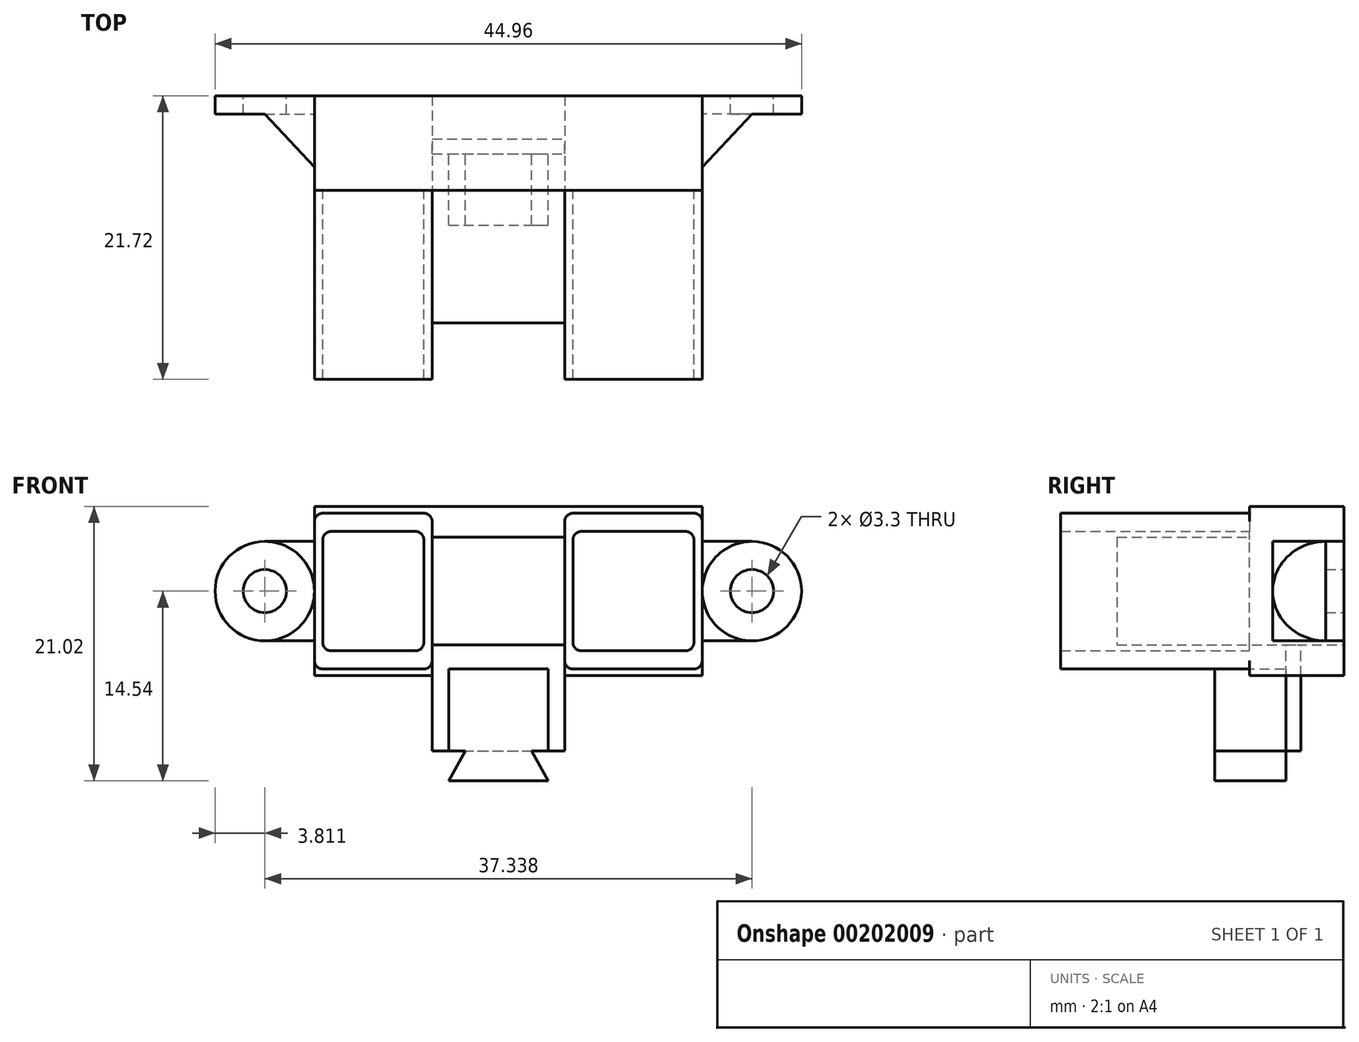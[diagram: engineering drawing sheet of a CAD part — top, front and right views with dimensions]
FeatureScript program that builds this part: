
annotation { "Feature Type Name" : "Feature", "Feature Type Description" : "" }
export const myFeature = defineFeature(function(context is Context, id is Id, definition is map)
    precondition{}
    {
        {
            var Q0;
            Q0=qCreatedBy(makeId("Front.planeOp"),FACE);
            var sketch = newSketch(context, id + "F0", { "sketchPlane" : qUnion([Q0])});
            skLineSegment(sketch, "E0.bottom", {"start": v(-14.86, 6.48) * mm, "end": v(14.86, 6.48) * mm});
            skLineSegment(sketch, "E0.top", {"start": v(-14.86, -6.48) * mm, "end": v(14.86, -6.48) * mm});
            skLineSegment(sketch, "E0.left", {"start": v(-14.86, 6.48) * mm, "end": v(-14.86, -6.48) * mm});
            skLineSegment(sketch, "E0.right", {"start": v(14.86, 6.48) * mm, "end": v(14.86, -6.48) * mm});
            skPoint(sketch, "E0.middle", {"position": v(0, 0) * mm});
            skSolve(sketch);
        }
        {
            var Q0;
            Q0=makeQuery(id+"F0.imprint","IMPRINT",FACE,{"disambiguationData":[TD([[makeQuery(id+"F0.imprint","IMPRINT",EDGE,{"derivedFrom":sQuery(id+"F0.wireOp",EDGE,"E0.bottom")}),-1.0]])]});
            extrude(context, id + "F1", {"entities" : qUnion([Q0]), "oppositeDirection" : true, "depth" : 7.24 * mm});
        }
        {
            var Q0;
            Q0=makeQuery(id+"F1.opExtrude","CAP_FACE",FACE,{"disambiguationData":[OSD([sQuery(id+"F0.wireOp",EDGE,"E0.bottom"),sQuery(id+"F0.wireOp",EDGE,"E0.top"),sQuery(id+"F0.wireOp",EDGE,"E0.left"),sQuery(id+"F0.wireOp",EDGE,"E0.right")])],"isStart":true});
            var sketch = newSketch(context, id + "F2", { "sketchPlane" : qUnion([Q0])});
            skLineSegment(sketch, "E1.bottom", {"start": v(-14.22, 5.97) * mm, "end": v(-6.48, 5.97) * mm});
            skLineSegment(sketch, "E1.top", {"start": v(-14.22, -5.97) * mm, "end": v(-6.48, -5.97) * mm});
            skLineSegment(sketch, "E1.left", {"start": v(-14.86, 5.33) * mm, "end": v(-14.86, -5.33) * mm});
            skLineSegment(sketch, "E1.right", {"start": v(-5.84, 5.33) * mm, "end": v(-5.84, -5.33) * mm});
            skPoint(sketch, "E2.visualSharp", {"position": v(-14.86, 5.97) * mm});
            skArc(sketch, "E2.filletArc", {"start": v(-14.22, 5.97) * mm, "mid": v(-14.67, 5.78) * mm, "end": v(-14.86, 5.33) * mm});
            skPoint(sketch, "E3.visualSharp", {"position": v(-5.84, 5.97) * mm});
            skArc(sketch, "E3.filletArc", {"start": v(-5.84, 5.33) * mm, "mid": v(-6.03, 5.78) * mm, "end": v(-6.48, 5.97) * mm});
            skPoint(sketch, "E4.visualSharp", {"position": v(-14.86, -5.97) * mm});
            skArc(sketch, "E4.filletArc", {"start": v(-14.86, -5.33) * mm, "mid": v(-14.67, -5.78) * mm, "end": v(-14.22, -5.97) * mm});
            skPoint(sketch, "E5.visualSharp", {"position": v(-5.84, -5.97) * mm});
            skArc(sketch, "E5.filletArc", {"start": v(-6.48, -5.97) * mm, "mid": v(-6.03, -5.78) * mm, "end": v(-5.84, -5.33) * mm});
            skLineSegment(sketch, "E6", {"start": v(-14.22, 3.94) * mm, "end": v(-14.22, -3.94) * mm});
            skLineSegment(sketch, "E7", {"start": v(-13.59, -4.57) * mm, "end": v(-7.11, -4.57) * mm});
            skLineSegment(sketch, "E8", {"start": v(-6.48, -3.94) * mm, "end": v(-6.48, 3.94) * mm});
            skLineSegment(sketch, "E9", {"start": v(-13.59, 4.57) * mm, "end": v(-7.11, 4.57) * mm});
            skPoint(sketch, "E10.visualSharp", {"position": v(-14.22, 4.57) * mm});
            skArc(sketch, "E10.filletArc", {"start": v(-13.59, 4.57) * mm, "mid": v(-14.04, 4.39) * mm, "end": v(-14.22, 3.94) * mm});
            skPoint(sketch, "E11.visualSharp", {"position": v(-6.48, 4.57) * mm});
            skArc(sketch, "E11.filletArc", {"start": v(-6.48, 3.94) * mm, "mid": v(-6.66, 4.39) * mm, "end": v(-7.11, 4.57) * mm});
            skPoint(sketch, "E12.visualSharp", {"position": v(-6.48, -4.57) * mm});
            skArc(sketch, "E12.filletArc", {"start": v(-7.11, -4.57) * mm, "mid": v(-6.66, -4.39) * mm, "end": v(-6.48, -3.94) * mm});
            skPoint(sketch, "E13.visualSharp", {"position": v(-14.22, -4.57) * mm});
            skArc(sketch, "E13.filletArc", {"start": v(-14.22, -3.94) * mm, "mid": v(-14.04, -4.39) * mm, "end": v(-13.59, -4.57) * mm});
            skSolve(sketch);
        }
        {
            var Q0;
            Q0=makeQuery(id+"F2.imprint","IMPRINT",FACE,{"disambiguationData":[TD([[makeQuery(id+"F2.imprint","IMPRINT",EDGE,{"derivedFrom":sQuery(id+"F2.wireOp",EDGE,"E1.bottom")}),-1.0]])]});
            extrude(context, id + "F3", {"entities" : qUnion([Q0]), "operationType" : NewBodyOperationType.ADD, "depth" : 14.48 * mm});
        }
        {
            var Q0;
            {var subQ0=sQuery(id+"F0.wireOp",EDGE,"E0.top");var subQ1=sQuery(id+"F0.wireOp",EDGE,"E0.bottom");var subQ2=sQuery(id+"F0.wireOp",EDGE,"E0.left");var subQ3=sQuery(id+"F0.wireOp",EDGE,"E0.right");Q0=makeQuery(id+"F3.boolean.opBoolean","SPLIT",FACE,{"disambiguationData":[TD([makeQuery(id+"F1.opExtrude","SWEPT_FACE",FACE,{"disambiguationData":[OSD([subQ1])]})])],"derivedFrom":makeQuery(id+"F1.opExtrude","CAP_FACE",FACE,{"disambiguationData":[OSD([subQ1,subQ0,subQ2,subQ3])],"isStart":true})});}
            var sketch = newSketch(context, id + "F4", { "sketchPlane" : qUnion([Q0])});
            skLineSegment(sketch, "E14.bottom", {"start": v(4.95, 5.97) * mm, "end": v(14.22, 5.97) * mm});
            skLineSegment(sketch, "E14.top", {"start": v(4.95, -5.97) * mm, "end": v(14.22, -5.97) * mm});
            skLineSegment(sketch, "E14.left", {"start": v(4.32, 5.33) * mm, "end": v(4.32, -5.33) * mm});
            skLineSegment(sketch, "E14.right", {"start": v(14.86, 5.33) * mm, "end": v(14.86, -5.33) * mm});
            skPoint(sketch, "E15.visualSharp", {"position": v(4.32, 5.97) * mm});
            skArc(sketch, "E15.filletArc", {"start": v(4.95, 5.97) * mm, "mid": v(4.5, 5.78) * mm, "end": v(4.32, 5.33) * mm});
            skPoint(sketch, "E16.visualSharp", {"position": v(14.86, 5.97) * mm});
            skArc(sketch, "E16.filletArc", {"start": v(14.86, 5.33) * mm, "mid": v(14.67, 5.78) * mm, "end": v(14.22, 5.97) * mm});
            skPoint(sketch, "E17.visualSharp", {"position": v(14.86, -5.97) * mm});
            skArc(sketch, "E17.filletArc", {"start": v(14.22, -5.97) * mm, "mid": v(14.67, -5.78) * mm, "end": v(14.86, -5.33) * mm});
            skPoint(sketch, "E18.visualSharp", {"position": v(4.32, -5.97) * mm});
            skArc(sketch, "E18.filletArc", {"start": v(4.32, -5.33) * mm, "mid": v(4.5, -5.78) * mm, "end": v(4.95, -5.97) * mm});
            skLineSegment(sketch, "E19", {"start": v(5.59, 4.57) * mm, "end": v(13.59, 4.57) * mm});
            skLineSegment(sketch, "E20", {"start": v(14.22, 3.94) * mm, "end": v(14.22, -3.94) * mm});
            skLineSegment(sketch, "E21", {"start": v(13.59, -4.57) * mm, "end": v(5.59, -4.57) * mm});
            skLineSegment(sketch, "E22", {"start": v(4.95, -3.94) * mm, "end": v(4.95, 3.94) * mm});
            skPoint(sketch, "E23.visualSharp", {"position": v(4.95, 4.57) * mm});
            skArc(sketch, "E23.filletArc", {"start": v(5.59, 4.57) * mm, "mid": v(5.14, 4.39) * mm, "end": v(4.95, 3.94) * mm});
            skPoint(sketch, "E24.visualSharp", {"position": v(14.22, 4.57) * mm});
            skArc(sketch, "E24.filletArc", {"start": v(14.22, 3.94) * mm, "mid": v(14.04, 4.39) * mm, "end": v(13.59, 4.57) * mm});
            skPoint(sketch, "E25.visualSharp", {"position": v(14.22, -4.57) * mm});
            skArc(sketch, "E25.filletArc", {"start": v(13.59, -4.57) * mm, "mid": v(14.04, -4.39) * mm, "end": v(14.22, -3.94) * mm});
            skPoint(sketch, "E26.visualSharp", {"position": v(4.95, -4.57) * mm});
            skArc(sketch, "E26.filletArc", {"start": v(4.95, -3.94) * mm, "mid": v(5.14, -4.39) * mm, "end": v(5.59, -4.57) * mm});
            skSolve(sketch);
        }
        {
            var Q0;
            Q0=makeQuery(id+"F4.imprint","IMPRINT",FACE,{"disambiguationData":[TD([[makeQuery(id+"F4.imprint","IMPRINT",EDGE,{"derivedFrom":sQuery(id+"F4.wireOp",EDGE,"E14.bottom")}),-1.0]])]});
            var Q1;
            Q1=makeQuery(id+"F3.opExtrude","CAP_FACE",FACE,{"disambiguationData":[OSD([sQuery(id+"F2.wireOp",EDGE,"E1.bottom"),sQuery(id+"F2.wireOp",EDGE,"E1.top"),sQuery(id+"F2.wireOp",EDGE,"E1.left"),sQuery(id+"F2.wireOp",EDGE,"E1.right"),sQuery(id+"F2.wireOp",EDGE,"E2.filletArc"),sQuery(id+"F2.wireOp",EDGE,"E3.filletArc"),sQuery(id+"F2.wireOp",EDGE,"E4.filletArc"),sQuery(id+"F2.wireOp",EDGE,"E5.filletArc"),sQuery(id+"F2.wireOp",EDGE,"E6"),sQuery(id+"F2.wireOp",EDGE,"E7"),sQuery(id+"F2.wireOp",EDGE,"E8"),sQuery(id+"F2.wireOp",EDGE,"E9"),sQuery(id+"F2.wireOp",EDGE,"E10.filletArc"),sQuery(id+"F2.wireOp",EDGE,"E11.filletArc"),sQuery(id+"F2.wireOp",EDGE,"E12.filletArc"),sQuery(id+"F2.wireOp",EDGE,"E13.filletArc")])],"isStart":false});
            extrude(context, id + "F5", {"entities" : qUnion([Q0]), "operationType" : NewBodyOperationType.ADD, "endBound" : BoundingType.UP_TO_SURFACE, "endBoundEntityFace" : qUnion([Q1]), "depth" : 25.4 * mm});
        }
        {
            var Q0;
            {var subQ5=sQuery(id+"F0.wireOp",EDGE,"E0.bottom");var subQ6=makeQuery(id+"F1.opExtrude","SWEPT_FACE",FACE,{"disambiguationData":[OSD([subQ5])]});var subQ8=sQuery(id+"F0.wireOp",EDGE,"E0.right");var subQ10=sQuery(id+"F0.wireOp",EDGE,"E0.top");var subQ12=sQuery(id+"F0.wireOp",EDGE,"E0.left");Q0=makeQuery(id+"F5.boolean.opBoolean","SPLIT",FACE,{"disambiguationData":[TD([subQ6])],"derivedFrom":makeQuery(id+"F3.boolean.opBoolean","SPLIT",FACE,{"disambiguationData":[TD([subQ6])],"derivedFrom":makeQuery(id+"F1.opExtrude","CAP_FACE",FACE,{"disambiguationData":[OSD([subQ5,subQ10,subQ12,subQ8])],"isStart":true})})});}
            var sketch = newSketch(context, id + "F6", { "sketchPlane" : qUnion([Q0])});
            skLineSegment(sketch, "E27.bottom", {"start": v(-5.84, 4.13) * mm, "end": v(4.32, 4.13) * mm});
            skLineSegment(sketch, "E27.top", {"start": v(-5.84, -4.13) * mm, "end": v(4.32, -4.13) * mm});
            skLineSegment(sketch, "E27.left", {"start": v(-5.84, 4.13) * mm, "end": v(-5.84, -4.13) * mm});
            skLineSegment(sketch, "E27.right", {"start": v(4.32, 4.13) * mm, "end": v(4.32, -4.13) * mm});
            skSolve(sketch);
        }
        {
            var Q0;
            Q0=makeQuery(id+"F6.imprint","IMPRINT",FACE,{"disambiguationData":[TD([[makeQuery(id+"F6.imprint","IMPRINT",EDGE,{"derivedFrom":sQuery(id+"F6.wireOp",EDGE,"E27.bottom")}),-1.0]])]});
            extrude(context, id + "F7", {"entities" : qUnion([Q0]), "operationType" : NewBodyOperationType.ADD, "depth" : 10.16 * mm});
        }
        {
            var Q0;
            Q0=makeQuery(id+"F1.opExtrude","CAP_FACE",FACE,{"disambiguationData":[OSD([sQuery(id+"F0.wireOp",EDGE,"E0.bottom"),sQuery(id+"F0.wireOp",EDGE,"E0.top"),sQuery(id+"F0.wireOp",EDGE,"E0.left"),sQuery(id+"F0.wireOp",EDGE,"E0.right")])],"isStart":false});
            var sketch = newSketch(context, id + "F8", { "sketchPlane" : qUnion([Q0])});
            skLineSegment(sketch, "E28", {"start": v(14.86, 0) * mm, "end": v(22.48, 0) * mm, "construction": true});
            skLineSegment(sketch, "E29", {"start": v(0, 6.48) * mm, "end": v(0, -6.48) * mm, "construction": true});
            skArc(sketch, "E30", {"start": v(18.67, -3.81) * mm, "mid": v(22.48, 0) * mm, "end": v(18.67, 3.8) * mm});
            skPoint(sketch, "E30.startSnap0", {"position": v(18.67, 0) * mm});
            skLineSegment(sketch, "E31", {"start": v(18.67, -3.8) * mm, "end": v(18.67, 3.8) * mm, "construction": true});
            skLineSegment(sketch, "E32", {"start": v(18.67, 3.8) * mm, "end": v(14.86, 3.8) * mm});
            skLineSegment(sketch, "E33", {"start": v(14.86, 3.8) * mm, "end": v(14.86, -3.81) * mm});
            skLineSegment(sketch, "E34", {"start": v(14.86, -3.81) * mm, "end": v(18.67, -3.8) * mm});
            skCircle(sketch, "E35", {"center": v(18.67, 0) * mm, "radius": 1.65 * mm});
            skLineSegment(sketch, "E36.MirrorCS", {"start": v(-18.67, 3.8) * mm, "end": v(-14.86, 3.8) * mm});
            skCircle(sketch, "E37.MirrorC", {"center": v(-18.67, 0) * mm, "radius": 1.65 * mm});
            skArc(sketch, "E38.MirrorCS", {"start": v(-18.67, -3.81) * mm, "mid": v(-22.48, 0) * mm, "end": v(-18.67, 3.8) * mm});
            skLineSegment(sketch, "E39.MirrorCS", {"start": v(-14.86, 3.8) * mm, "end": v(-14.86, -3.81) * mm});
            skLineSegment(sketch, "E40.MirrorCS", {"start": v(-14.86, -3.81) * mm, "end": v(-18.67, -3.81) * mm});
            skSolve(sketch);
        }
        {
            var Q0;
            Q0=makeQuery(id+"F8.imprint","IMPRINT",FACE,{"disambiguationData":[TD([[makeQuery(id+"F8.imprint","IMPRINT",EDGE,{"derivedFrom":sQuery(id+"F8.wireOp",EDGE,"E30")}),1.0]])]});
            var Q1;
            Q1=makeQuery(id+"F8.imprint","IMPRINT",FACE,{"disambiguationData":[TD([[makeQuery(id+"F8.imprint","IMPRINT",EDGE,{"derivedFrom":sQuery(id+"F8.wireOp",EDGE,"E36.MirrorCS")}),-1.0]])]});
            extrude(context, id + "F9", {"entities" : qUnion([Q0, Q1]), "operationType" : NewBodyOperationType.ADD, "oppositeDirection" : true, "depth" : 5.46 * mm});
        }
        {
            var Q0;
            Q0=makeQuery(id+"F9.opExtrude","SWEPT_FACE",FACE,{"disambiguationData":[OSD([sQuery(id+"F8.wireOp",EDGE,"E36.MirrorCS")])]});
            var sketch = newSketch(context, id + "F10", { "sketchPlane" : qUnion([Q0])});
            skLineSegment(sketch, "E41", {"start": v(0, 0) * mm, "end": v(0, 17.62) * mm, "construction": true});
            skLineSegment(sketch, "E42", {"start": v(18.67, 5.84) * mm, "end": v(14.86, 1.78) * mm});
            skLineSegment(sketch, "E43", {"start": v(14.86, 1.78) * mm, "end": v(14.86, 1.78) * mm});
            skLineSegment(sketch, "E44", {"start": v(14.86, 1.78) * mm, "end": v(22.48, 1.78) * mm});
            skLineSegment(sketch, "E45", {"start": v(22.48, 1.78) * mm, "end": v(22.48, 5.84) * mm});
            skLineSegment(sketch, "E46", {"start": v(22.48, 5.84) * mm, "end": v(18.67, 5.84) * mm});
            skLineSegment(sketch, "E47.MirrorCS", {"start": v(-14.86, 1.78) * mm, "end": v(-22.48, 1.78) * mm});
            skLineSegment(sketch, "E48.MirrorCS", {"start": v(-22.48, 1.78) * mm, "end": v(-22.48, 5.84) * mm});
            skLineSegment(sketch, "E49.MirrorCS", {"start": v(-18.67, 5.84) * mm, "end": v(-14.86, 1.78) * mm});
            skLineSegment(sketch, "E50.MirrorCS", {"start": v(-22.48, 5.84) * mm, "end": v(-18.67, 5.84) * mm});
            skSolve(sketch);
        }
        {
            var Q0;
            Q0=makeQuery(id+"F10.imprint","IMPRINT",FACE,{"disambiguationData":[TD([[makeQuery(id+"F10.imprint","IMPRINT",EDGE,{"derivedFrom":sQuery(id+"F10.wireOp",EDGE,"E47.MirrorCS")}),-1.0]])]});
            var Q1;
            {var subQ3=sQuery(id+"F10.wireOp",EDGE,"E45");Q1=makeQuery(id+"F10.imprint","IMPRINT",FACE,{"disambiguationData":[TD([[makeQuery(id+"F10.imprint","IMPRINT",EDGE,{"derivedFrom":subQ3}),1.0]])]});}
            var Q2;
            {var subQ0=sQuery(id+"F10.wireOp",EDGE,"E42");Q2=makeQuery(id+"F10.imprint","IMPRINT",FACE,{"disambiguationData":[TD([[makeQuery(id+"F10.imprint","IMPRINT",EDGE,{"derivedFrom":subQ0}),1.0]])]});}
            extrude(context, id + "F11", {"entities" : qUnion([Q0, Q1, Q2]), "operationType" : NewBodyOperationType.REMOVE, "endBound" : BoundingType.THROUGH_ALL, "oppositeDirection" : true, "depth" : 25.4 * mm});
        }
        {
            var Q0;
            Q0=makeQuery(id+"F11.boolean.opBoolean","COPY",FACE,{"derivedFrom":makeQuery(id+"F11.opExtrude","SWEPT_FACE",FACE,{"disambiguationData":[OSD([sQuery(id+"F10.wireOp",EDGE,"E46")])]})});
            var sketch = newSketch(context, id + "F12", { "sketchPlane" : qUnion([Q0])});
            skCircle(sketch, "E51", {"center": v(18.67, 0) * mm, "radius": 3.8 * mm});
            skLineSegment(sketch, "E52", {"start": v(0, 6.52) * mm, "end": v(0, -6.57) * mm, "construction": true});
            skCircle(sketch, "E53.MirrorC", {"center": v(-18.67, 0) * mm, "radius": 3.8 * mm});
            skSolve(sketch);
        }
        {
            var Q0;
            Q0 = qSketchRegion(id + "F12", true);
            extrude(context, id + "F13", {"entities" : qUnion([Q0]), "operationType" : NewBodyOperationType.REMOVE, "endBound" : BoundingType.THROUGH_ALL, "depth" : 25.4 * mm});
        }
        {
            var Q0;
            {var subQ9=sQuery(id+"F0.wireOp",EDGE,"E0.top");var subQ10=makeQuery(id+"F1.opExtrude","SWEPT_FACE",FACE,{"disambiguationData":[OSD([subQ9])]});var subQ11=sQuery(id+"F0.wireOp",EDGE,"E0.left");var subQ13=sQuery(id+"F0.wireOp",EDGE,"E0.right");var subQ18=sQuery(id+"F0.wireOp",EDGE,"E0.bottom");var subQ19=makeQuery(id+"F1.opExtrude","SWEPT_FACE",FACE,{"disambiguationData":[OSD([subQ18])]});Q0=makeQuery(id+"F7.boolean.opBoolean","SPLIT",FACE,{"disambiguationData":[TD([subQ10])],"derivedFrom":makeQuery(id+"F5.boolean.opBoolean","SPLIT",FACE,{"disambiguationData":[TD([subQ19])],"derivedFrom":makeQuery(id+"F3.boolean.opBoolean","SPLIT",FACE,{"disambiguationData":[TD([subQ19])],"derivedFrom":makeQuery(id+"F1.opExtrude","CAP_FACE",FACE,{"disambiguationData":[OSD([subQ18,subQ9,subQ11,subQ13])],"isStart":true})})})});}
            var sketch = newSketch(context, id + "F14", { "sketchPlane" : qUnion([Q0])});
            skLineSegment(sketch, "E54.bottom", {"start": v(-5.84, -4.13) * mm, "end": v(4.32, -4.13) * mm});
            skLineSegment(sketch, "E54.top", {"start": v(-5.84, -6.48) * mm, "end": v(4.32, -6.48) * mm});
            skLineSegment(sketch, "E54.left", {"start": v(-5.84, -4.13) * mm, "end": v(-5.84, -6.48) * mm});
            skLineSegment(sketch, "E54.right", {"start": v(4.32, -4.13) * mm, "end": v(4.32, -6.48) * mm});
            skSolve(sketch);
        }
        {
            var Q0;
            {var subQ2=sQuery(id+"F14.wireOp",EDGE,"E54.bottom");Q0=makeQuery(id+"F14.imprint","IMPRINT",FACE,{"disambiguationData":[TD([[makeQuery(id+"F14.imprint","IMPRINT",EDGE,{"derivedFrom":subQ2}),-1.0]])]});}
            extrude(context, id + "F15", {"entities" : qUnion([Q0]), "operationType" : NewBodyOperationType.REMOVE, "endBound" : BoundingType.THROUGH_ALL, "oppositeDirection" : true, "depth" : 25.4 * mm});
        }
        {
            var Q0;
            Q0=makeQuery(id+"F15.boolean.opBoolean","MERGE",FACE,{"derivedFrom":[makeQuery(id+"F7.opExtrude","SWEPT_FACE",FACE,{"disambiguationData":[OSD([sQuery(id+"F6.wireOp",EDGE,"E27.top")])]}),makeQuery(id+"F15.opExtrude","SWEPT_FACE",FACE,{"disambiguationData":[OSD([sQuery(id+"F14.wireOp",EDGE,"E54.bottom")])]})]});
            var sketch = newSketch(context, id + "F16", { "sketchPlane" : qUnion([Q0])});
            skLineSegment(sketch, "E55.bottom", {"start": v(-5.84, -2.8) * mm, "end": v(4.32, -2.8) * mm});
            skLineSegment(sketch, "E55.top", {"start": v(-5.84, -3.94) * mm, "end": v(4.32, -3.94) * mm});
            skLineSegment(sketch, "E55.left", {"start": v(-5.84, -2.8) * mm, "end": v(-5.84, -3.94) * mm});
            skLineSegment(sketch, "E55.right", {"start": v(4.32, -2.8) * mm, "end": v(4.32, -3.94) * mm});
            skSolve(sketch);
        }
        {
            var Q0;
            Q0=makeQuery(id+"F16.imprint","IMPRINT",FACE,{"disambiguationData":[TD([[makeQuery(id+"F16.imprint","IMPRINT",EDGE,{"derivedFrom":sQuery(id+"F16.wireOp",EDGE,"E55.bottom")}),-1.0]])]});
            extrude(context, id + "F17", {"entities" : qUnion([Q0]), "depth" : 8.13 * mm});
        }
        {
            var Q0;
            Q0=makeQuery(id+"F17.opExtrude","SWEPT_FACE",FACE,{"disambiguationData":[OSD([sQuery(id+"F16.wireOp",EDGE,"E55.bottom")])]});
            var sketch = newSketch(context, id + "F18", { "sketchPlane" : qUnion([Q0])});
            skLineSegment(sketch, "E56.bottom", {"start": v(-4.57, -5.97) * mm, "end": v(3.05, -5.97) * mm});
            skLineSegment(sketch, "E56.top", {"start": v(-4.57, -12.26) * mm, "end": v(3.05, -12.26) * mm});
            skLineSegment(sketch, "E56.left", {"start": v(-4.57, -5.97) * mm, "end": v(-4.57, -12.26) * mm});
            skLineSegment(sketch, "E56.right", {"start": v(3.05, -5.97) * mm, "end": v(3.05, -12.26) * mm});
            skLineSegment(sketch, "E57.bottom", {"start": v(3.05, -5.97) * mm, "end": v(1.78, -5.97) * mm});
            skLineSegment(sketch, "E57.top", {"start": v(3.05, -4.13) * mm, "end": v(1.78, -4.13) * mm});
            skLineSegment(sketch, "E57.left", {"start": v(3.05, -5.97) * mm, "end": v(3.05, -4.13) * mm});
            skLineSegment(sketch, "E57.right", {"start": v(1.78, -5.97) * mm, "end": v(1.78, -4.13) * mm});
            skLineSegment(sketch, "E58", {"start": v(-0.76, -12.26) * mm, "end": v(-0.76, -4.13) * mm, "construction": true});
            skLineSegment(sketch, "E59.MirrorCS", {"start": v(-4.57, -5.97) * mm, "end": v(-3.3, -5.97) * mm});
            skLineSegment(sketch, "E60.MirrorCS", {"start": v(-3.3, -5.97) * mm, "end": v(-3.3, -4.13) * mm});
            skLineSegment(sketch, "E61.MirrorCS", {"start": v(-4.57, -5.97) * mm, "end": v(-4.57, -4.13) * mm});
            skLineSegment(sketch, "E62.MirrorCS", {"start": v(-4.57, -4.13) * mm, "end": v(-3.3, -4.13) * mm});
            skLineSegment(sketch, "E63", {"start": v(1.78, -12.26) * mm, "end": v(3.05, -14.54) * mm});
            skLineSegment(sketch, "E64", {"start": v(3.05, -14.54) * mm, "end": v(-4.57, -14.54) * mm});
            skLineSegment(sketch, "E65", {"start": v(1.78, -12.26) * mm, "end": v(-3.3, -12.26) * mm});
            skLineSegment(sketch, "E66", {"start": v(-3.3, -12.26) * mm, "end": v(-4.57, -14.54) * mm});
            skSolve(sketch);
        }
        {
            var Q0;
            Q0=makeQuery(id+"F18.imprint","IMPRINT",FACE,{"disambiguationData":[TD([[makeQuery(id+"F18.imprint","IMPRINT",EDGE,{"derivedFrom":sQuery(id+"F18.wireOp",EDGE,"E56.bottom")}),-1.0]])]});
            var Q1;
            Q1=makeQuery(id+"F18.imprint","IMPRINT",FACE,{"disambiguationData":[TD([[makeQuery(id+"F18.imprint","IMPRINT",EDGE,{"derivedFrom":sQuery(id+"F18.wireOp",EDGE,"E59.MirrorCS")}),1.0]])]});
            var Q2;
            Q2=makeQuery(id+"F18.imprint","IMPRINT",FACE,{"disambiguationData":[TD([[makeQuery(id+"F18.imprint","IMPRINT",EDGE,{"derivedFrom":sQuery(id+"F18.wireOp",EDGE,"E57.bottom")}),-1.0]])]});
            var Q3;
            Q3=makeQuery(id+"F18.imprint","IMPRINT",FACE,{"disambiguationData":[TD([[makeQuery(id+"F18.imprint","IMPRINT",EDGE,{"derivedFrom":sQuery(id+"F18.wireOp",EDGE,"E63")}),-1.0]])]});
            extrude(context, id + "F19", {"entities" : qUnion([Q0, Q1, Q2, Q3]), "depth" : 5.46 * mm});
        }
    });
